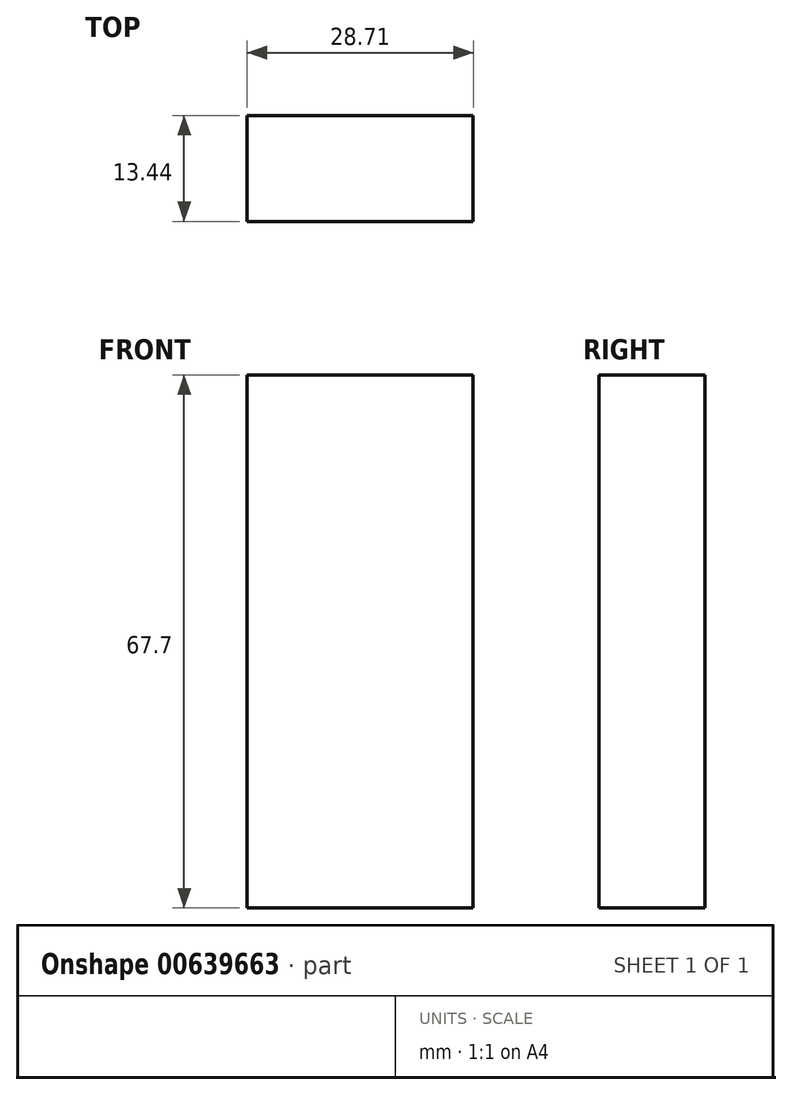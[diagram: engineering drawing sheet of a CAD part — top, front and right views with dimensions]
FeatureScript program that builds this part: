
annotation { "Feature Type Name" : "Feature", "Feature Type Description" : "" }
export const myFeature = defineFeature(function(context is Context, id is Id, definition is map)
    precondition{}
    {
        {
            var Q0;
            Q0=qCreatedBy(makeId("Top.planeOp"),FACE);
            var sketch = newSketch(context, id + "F0", { "sketchPlane" : qUnion([Q0])});
            skLineSegment(sketch, "E0.bottom", {"start": v(0, 0) * mm, "end": v(28.7, 0) * mm});
            skLineSegment(sketch, "E0.top", {"start": v(0, -13.44) * mm, "end": v(28.7, -13.44) * mm});
            skLineSegment(sketch, "E0.left", {"start": v(0, 0) * mm, "end": v(0, -13.44) * mm});
            skLineSegment(sketch, "E0.right", {"start": v(28.7, 0) * mm, "end": v(28.7, -13.44) * mm});
            skSolve(sketch);
        }
        {
            var Q0;
            Q0=makeQuery(id+"F0.imprint","IMPRINT",FACE,{"disambiguationData":[TD([[makeQuery(id+"F0.imprint","IMPRINT",EDGE,{"derivedFrom":sQuery(id+"F0.wireOp",EDGE,"E0.bottom")}),-1.0]])]});
            extrude(context, id + "F1", {"entities" : qUnion([Q0]), "depth" : 67.7 * mm, "offsetDistance" : 25 * mm});
        }
    });
